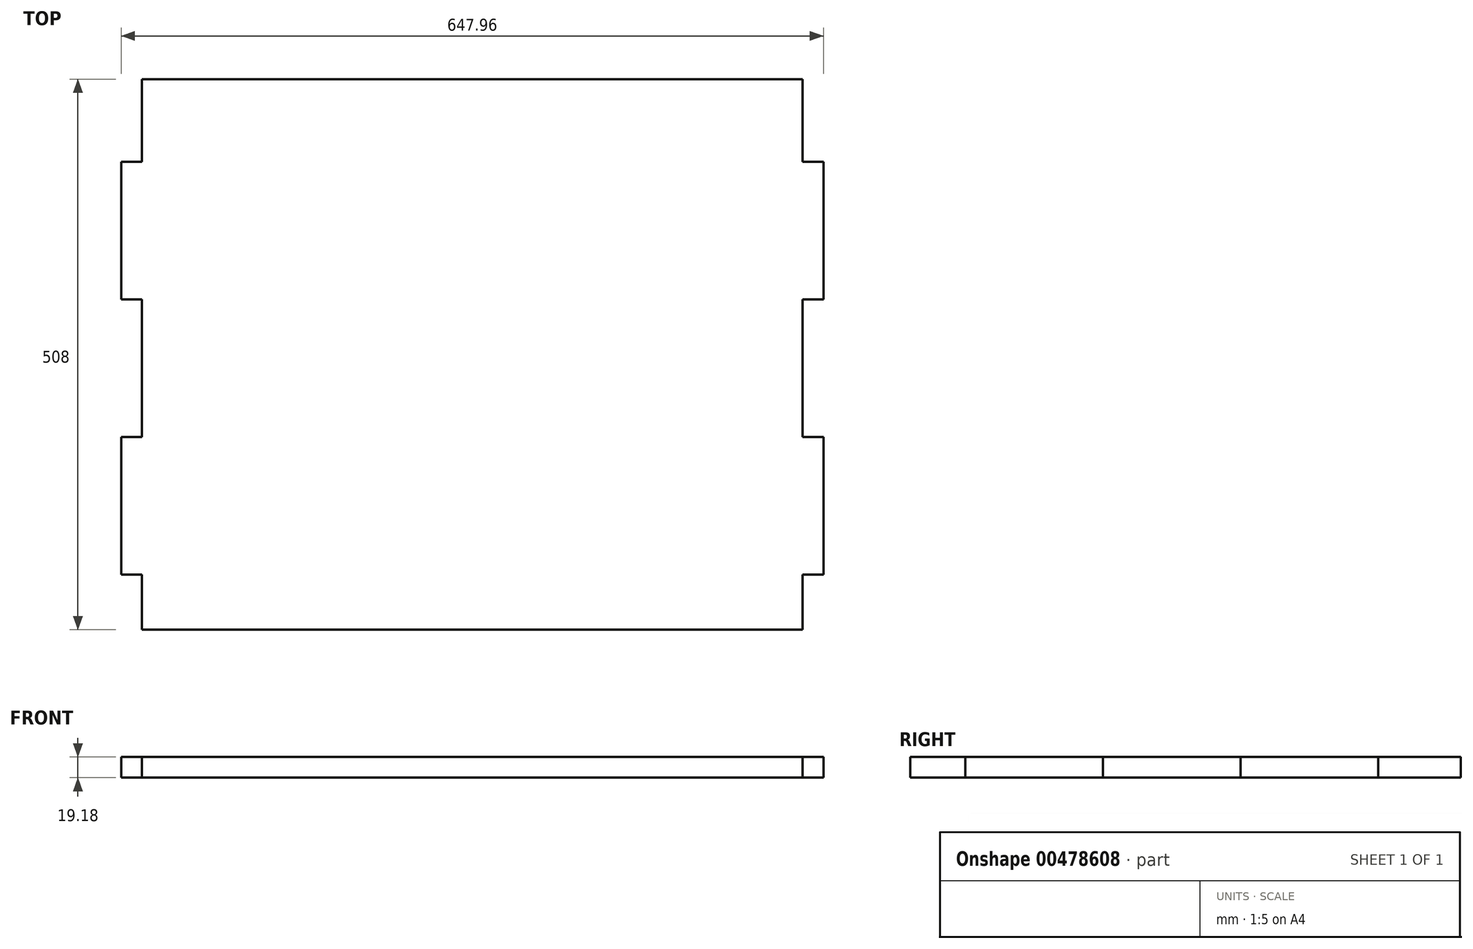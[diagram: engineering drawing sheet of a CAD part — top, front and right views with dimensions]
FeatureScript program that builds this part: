
annotation { "Feature Type Name" : "Feature", "Feature Type Description" : "" }
export const myFeature = defineFeature(function(context is Context, id is Id, definition is map)
    precondition{}
    {
        {
            var Q0;
            Q0=qCreatedBy(makeId("Top.planeOp"),FACE);
            var sketch = newSketch(context, id + "F0", { "sketchPlane" : qUnion([Q0])});
            skLineSegment(sketch, "E0.bottom", {"start": v(-228.6, 266.7) * mm, "end": v(381, 266.7) * mm});
            skLineSegment(sketch, "E0.top", {"start": v(-228.6, -241.3) * mm, "end": v(381, -241.3) * mm});
            skLineSegment(sketch, "E0.left", {"start": v(-228.6, 266.7) * mm, "end": v(-228.6, -241.3) * mm});
            skLineSegment(sketch, "E0.right", {"start": v(381, 266.7) * mm, "end": v(381, -241.3) * mm});
            skLineSegment(sketch, "E1", {"start": v(381, 190.5) * mm, "end": v(400.18, 190.5) * mm});
            skLineSegment(sketch, "E2", {"start": v(400.18, 190.5) * mm, "end": v(400.18, 63.5) * mm});
            skLineSegment(sketch, "E3", {"start": v(400.18, 63.5) * mm, "end": v(381, 63.5) * mm});
            skLineSegment(sketch, "E4.bottom", {"start": v(381, -63.5) * mm, "end": v(400.18, -63.5) * mm});
            skLineSegment(sketch, "E5", {"start": v(400.18, -63.5) * mm, "end": v(400.18, -190.5) * mm});
            skLineSegment(sketch, "E6", {"start": v(400.18, -190.5) * mm, "end": v(381, -190.5) * mm});
            skLineSegment(sketch, "E7", {"start": v(-228.6, 190.5) * mm, "end": v(-247.78, 190.5) * mm});
            skLineSegment(sketch, "E8", {"start": v(-247.78, 190.5) * mm, "end": v(-247.78, 63.5) * mm});
            skLineSegment(sketch, "E9", {"start": v(-247.78, 63.5) * mm, "end": v(-228.6, 63.5) * mm});
            skLineSegment(sketch, "E10", {"start": v(-228.6, -63.5) * mm, "end": v(-247.78, -63.5) * mm});
            skLineSegment(sketch, "E11", {"start": v(-247.78, -63.5) * mm, "end": v(-247.78, -190.5) * mm});
            skLineSegment(sketch, "E12", {"start": v(-247.78, -190.5) * mm, "end": v(-228.6, -190.5) * mm});
            skSolve(sketch);
        }
        {
            var Q0;
            {var subQ0=sQuery(id+"F0.wireOp",EDGE,"E7");Q0=makeQuery(id+"F0.imprint","IMPRINT",FACE,{"disambiguationData":[TD([[makeQuery(id+"F0.imprint","IMPRINT",EDGE,{"derivedFrom":subQ0}),1.0]])]});}
            var Q1;
            {var subQ0=sQuery(id+"F0.wireOp",EDGE,"E10");Q1=makeQuery(id+"F0.imprint","IMPRINT",FACE,{"disambiguationData":[TD([[makeQuery(id+"F0.imprint","IMPRINT",EDGE,{"derivedFrom":subQ0}),1.0]])]});}
            var Q2;
            {var subQ0=sQuery(id+"F0.wireOp",EDGE,"E4.bottom");Q2=makeQuery(id+"F0.imprint","IMPRINT",FACE,{"disambiguationData":[TD([[makeQuery(id+"F0.imprint","IMPRINT",EDGE,{"derivedFrom":subQ0}),-1.0]])]});}
            var Q3;
            {var subQ0=sQuery(id+"F0.wireOp",EDGE,"E1");Q3=makeQuery(id+"F0.imprint","IMPRINT",FACE,{"disambiguationData":[TD([[makeQuery(id+"F0.imprint","IMPRINT",EDGE,{"derivedFrom":subQ0}),-1.0]])]});}
            var Q4;
            {var subQ4=sQuery(id+"F0.wireOp",EDGE,"E0.bottom");Q4=makeQuery(id+"F0.imprint","IMPRINT",FACE,{"disambiguationData":[TD([[makeQuery(id+"F0.imprint","IMPRINT",EDGE,{"derivedFrom":subQ4}),-1.0]])]});}
            extrude(context, id + "F1", {"entities" : qUnion([Q0, Q1, Q2, Q3, Q4]), "depth" : 19.18 * mm, "offsetDistance" : 25.4 * mm});
        }
    });
